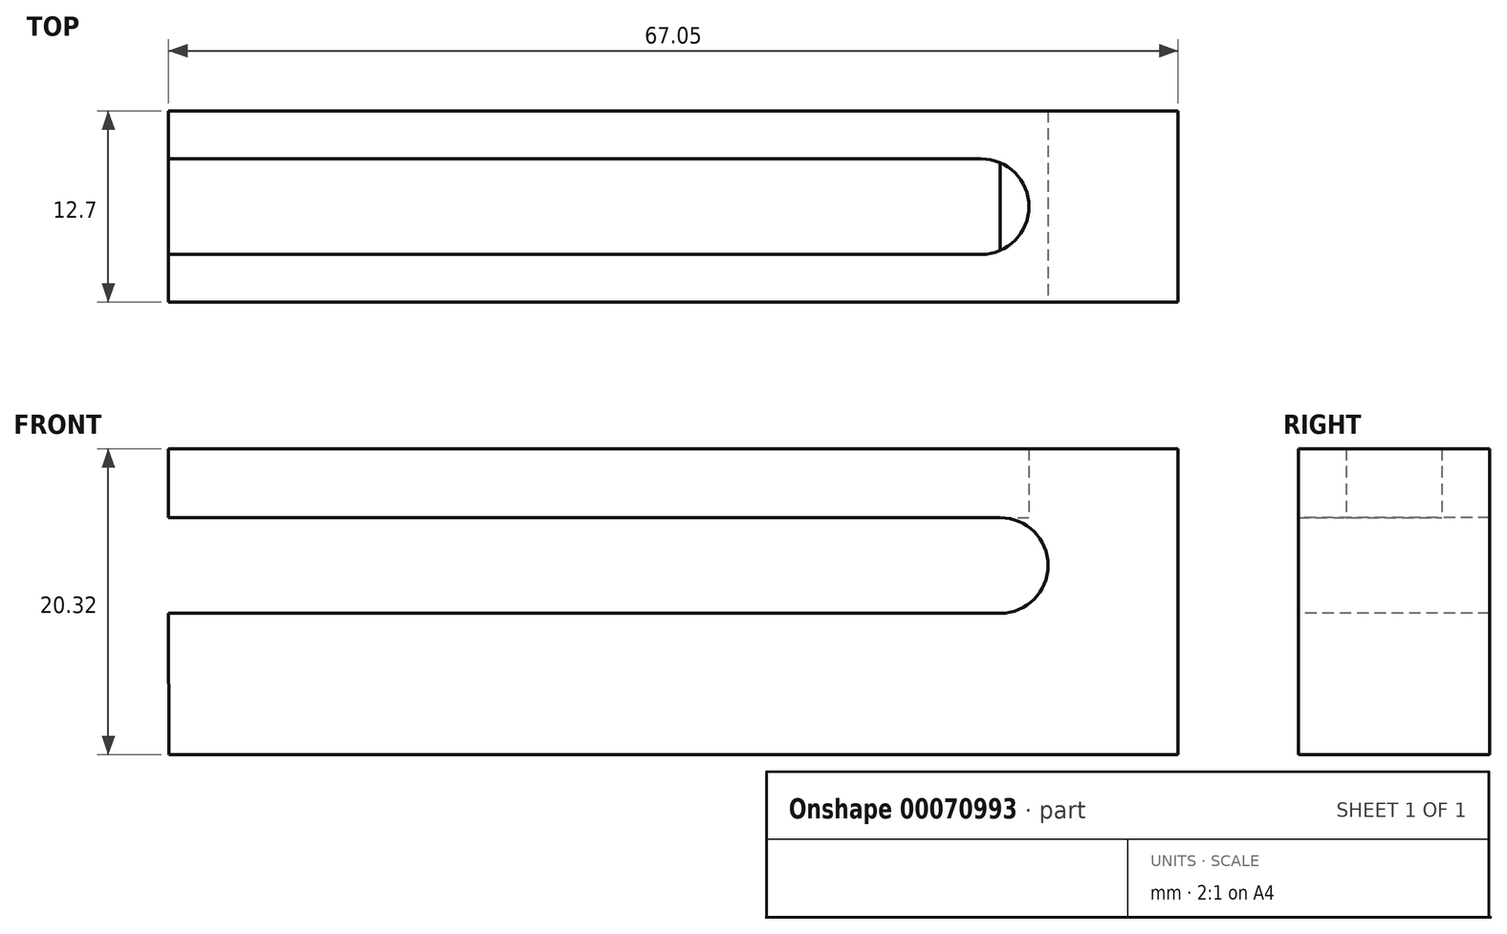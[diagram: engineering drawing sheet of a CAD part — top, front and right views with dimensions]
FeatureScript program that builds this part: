
annotation { "Feature Type Name" : "Feature", "Feature Type Description" : "" }
export const myFeature = defineFeature(function(context is Context, id is Id, definition is map)
    precondition{}
    {
        {
            var Q0;
            Q0=qCreatedBy(makeId("Top.planeOp"),FACE);
            var sketch = newSketch(context, id + "F0", { "sketchPlane" : qUnion([Q0])});
            skLineSegment(sketch, "E0.bottom", {"start": v(-43, 5.27) * mm, "end": v(24.05, 5.27) * mm});
            skLineSegment(sketch, "E0.top", {"start": v(-43, -7.43) * mm, "end": v(24.05, -7.43) * mm});
            skLineSegment(sketch, "E0.right", {"start": v(24.05, 5.27) * mm, "end": v(24.05, -7.43) * mm});
            skLineSegment(sketch, "E1", {"start": v(-43, 5.27) * mm, "end": v(-43, 2.1) * mm});
            skLineSegment(sketch, "E2", {"start": v(-43, -7.43) * mm, "end": v(-43, -4.25) * mm});
            skLineSegment(sketch, "E3", {"start": v(-43, 2.1) * mm, "end": v(10.97, 2.1) * mm});
            skLineSegment(sketch, "E4", {"start": v(-43, -4.25) * mm, "end": v(10.97, -4.25) * mm});
            skArc(sketch, "E5", {"start": v(10.97, 2.1) * mm, "mid": v(14.15, -1.08) * mm, "end": v(10.97, -4.25) * mm});
            skSolve(sketch);
        }
        {
            var Q0;
            Q0=makeQuery(id+"F0.imprint","IMPRINT",FACE,{"disambiguationData":[TD([[makeQuery(id+"F0.imprint","IMPRINT",EDGE,{"derivedFrom":sQuery(id+"F0.wireOp",EDGE,"E0.bottom")}),-1.0]])]});
            extrude(context, id + "F1", {"entities" : qUnion([Q0]), "depth" : 4.57 * mm});
        }
        {
            var Q0;
            Q0=makeQuery(id+"F1.opExtrude","SWEPT_FACE",FACE,{"disambiguationData":[OSD([sQuery(id+"F0.wireOp",EDGE,"E0.top")])]});
            var sketch = newSketch(context, id + "F2", { "sketchPlane" : qUnion([Q0])});
            skLineSegment(sketch, "E6", {"start": v(-43, 0) * mm, "end": v(12.24, 0) * mm});
            skLineSegment(sketch, "E7", {"start": v(-43, -6.35) * mm, "end": v(12.24, -6.35) * mm});
            skArc(sketch, "E8", {"start": v(12.24, 0) * mm, "mid": v(15.42, -3.17) * mm, "end": v(12.24, -6.35) * mm});
            skLineSegment(sketch, "E9.bottom", {"start": v(24.05, 0) * mm, "end": v(-43, 0) * mm});
            skLineSegment(sketch, "E9.top", {"start": v(24.05, -15.75) * mm, "end": v(-43, -15.75) * mm});
            skLineSegment(sketch, "E9.left", {"start": v(24.05, 0) * mm, "end": v(24.05, -15.75) * mm});
            skLineSegment(sketch, "E10", {"start": v(-43, -15.75) * mm, "end": v(-43, -6.35) * mm});
            skSolve(sketch);
        }
        {
            var Q0;
            Q0=makeQuery(id+"F2.imprint","IMPRINT",FACE,{"disambiguationData":[TD([[makeQuery(id+"F2.imprint","IMPRINT",EDGE,{"derivedFrom":sQuery(id+"F2.wireOp",EDGE,"E7")}),-1.0]])]});
            extrude(context, id + "F3", {"entities" : qUnion([Q0]), "operationType" : NewBodyOperationType.ADD, "oppositeDirection" : true, "depth" : 12.7 * mm});
        }
        {
            var Q0;
            Q0=makeQuery(id+"F1.opExtrude","SWEPT_BODY",BODY,{"disambiguationData":[OSD([sQuery(id+"F0.wireOp",EDGE,"E0.bottom"),sQuery(id+"F0.wireOp",EDGE,"E0.top"),sQuery(id+"F0.wireOp",EDGE,"E0.right"),sQuery(id+"F0.wireOp",EDGE,"E1"),sQuery(id+"F0.wireOp",EDGE,"E2"),sQuery(id+"F0.wireOp",EDGE,"E3"),sQuery(id+"F0.wireOp",EDGE,"E4"),sQuery(id+"F0.wireOp",EDGE,"E5")])]});
            transform(context, id + "F4", {"entities" : qUnion([Q0]), "transformType" : TransformType.TRANSLATION_3D, "dx" : 43 * mm, "dy" : 7.42 * mm, "dz" : 15.75 * mm, "makeCopy" : false});
        }
    });
